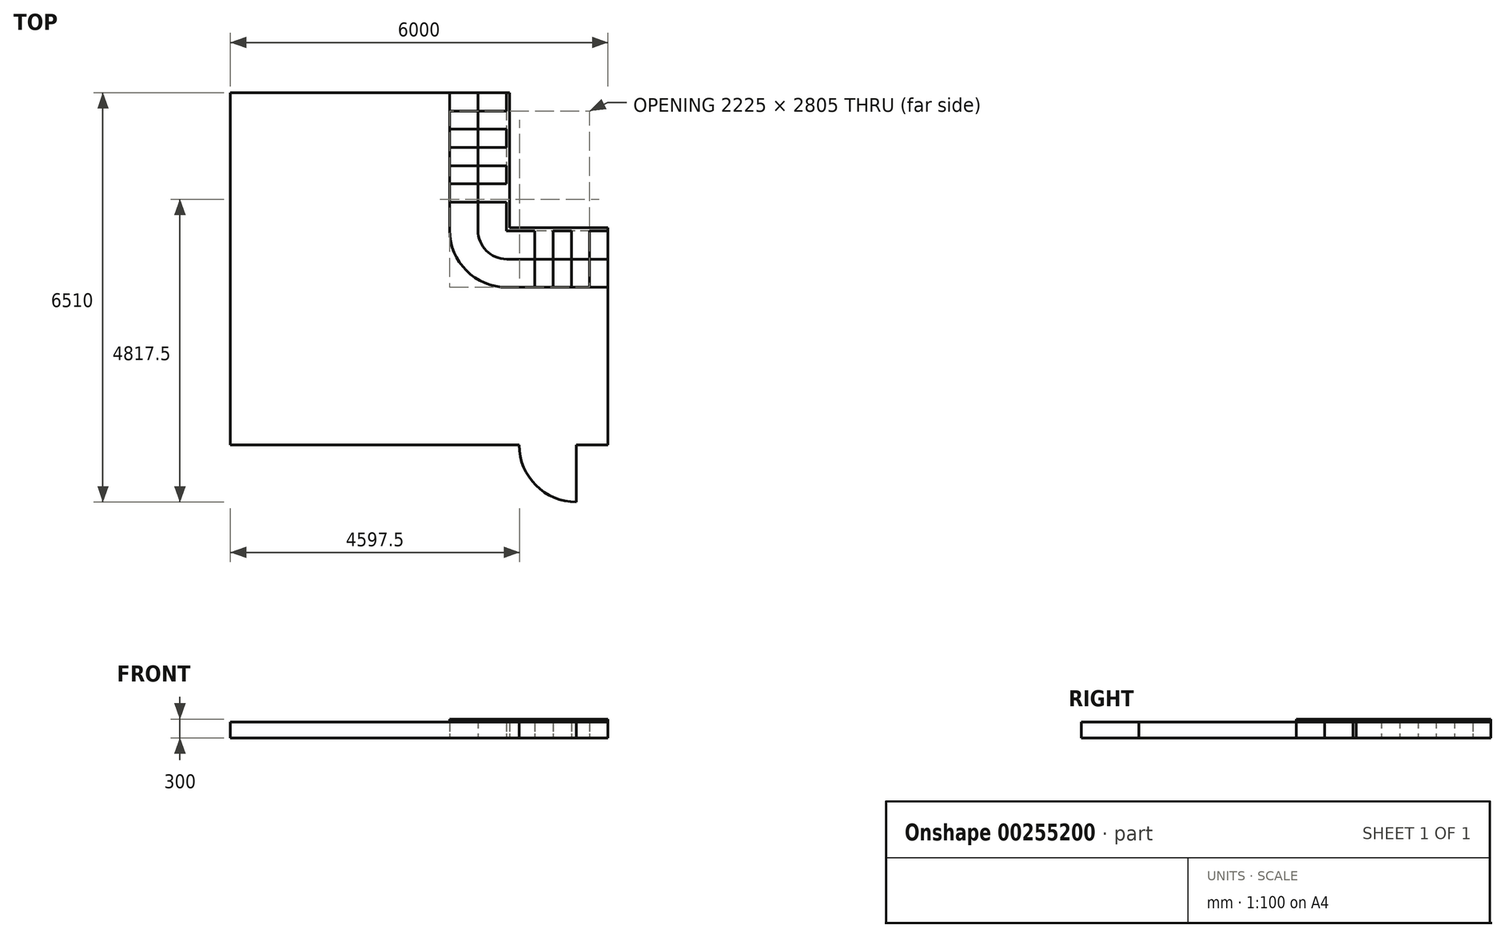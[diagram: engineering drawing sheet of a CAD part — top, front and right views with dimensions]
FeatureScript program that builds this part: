
annotation { "Feature Type Name" : "Feature", "Feature Type Description" : "" }
export const myFeature = defineFeature(function(context is Context, id is Id, definition is map)
    precondition{}
    {
        {
            var Q0;
            Q0=qCreatedBy(makeId("Top.planeOp"),FACE);
            var sketch = newSketch(context, id + "F0", { "sketchPlane" : qUnion([Q0])});
            skLineSegment(sketch, "E0", {"start": v(-4021.26, -49.2) * mm, "end": v(568.74, -49.2) * mm});
            skLineSegment(sketch, "E1", {"start": v(-4021.26, -49.2) * mm, "end": v(-4021.26, 5550.8) * mm});
            skLineSegment(sketch, "E2", {"start": v(-4021.26, 5550.8) * mm, "end": v(-536.26, 5550.8) * mm});
            skLineSegment(sketch, "E3", {"start": v(-536.26, 5550.8) * mm, "end": v(-86.26, 5550.8) * mm});
            skLineSegment(sketch, "E4", {"start": v(-86.26, 5550.8) * mm, "end": v(363.74, 5550.8) * mm});
            skLineSegment(sketch, "E5", {"start": v(-86.26, 5550.8) * mm, "end": v(-86.26, 3810.8) * mm});
            skLineSegment(sketch, "E6", {"start": v(363.74, 5550.8) * mm, "end": v(363.74, 3810.8) * mm});
            skLineSegment(sketch, "E7", {"start": v(363.74, 5550.8) * mm, "end": v(413.74, 5550.8) * mm});
            skLineSegment(sketch, "E8", {"start": v(413.74, 5550.8) * mm, "end": v(413.74, 3810.8) * mm});
            skPoint(sketch, "E9.end.orphan", {"position": v(-536.26, 3810.8) * mm});
            skPoint(sketch, "E10", {"position": v(-536.26, 5260.8) * mm});
            skPoint(sketch, "E11", {"position": v(-536.26, 5550.8) * mm});
            skPoint(sketch, "E12", {"position": v(-536.26, 4970.8) * mm});
            skPoint(sketch, "E13", {"position": v(-536.26, 4680.8) * mm});
            skPoint(sketch, "E14", {"position": v(-536.26, 4390.8) * mm});
            skPoint(sketch, "E15", {"position": v(-536.26, 4100.8) * mm});
            skLineSegment(sketch, "E16", {"start": v(-536.26, 5550.8) * mm, "end": v(-536.26, 3810.8) * mm});
            skLineSegment(sketch, "E17", {"start": v(-536.26, 5260.8) * mm, "end": v(363.74, 5260.8) * mm});
            skLineSegment(sketch, "E18", {"start": v(-536.26, 4970.8) * mm, "end": v(363.74, 4970.8) * mm});
            skLineSegment(sketch, "E19", {"start": v(-536.26, 4680.8) * mm, "end": v(363.74, 4680.8) * mm});
            skLineSegment(sketch, "E20", {"start": v(-536.26, 4390.8) * mm, "end": v(363.74, 4390.8) * mm});
            skLineSegment(sketch, "E21", {"start": v(-536.26, 4100.8) * mm, "end": v(363.74, 4100.8) * mm});
            skLineSegment(sketch, "E22", {"start": v(-536.26, 3810.8) * mm, "end": v(363.74, 3810.8) * mm});
            skLineSegment(sketch, "E23", {"start": v(1478.74, -49.2) * mm, "end": v(1978.74, -49.2) * mm});
            skLineSegment(sketch, "E24", {"start": v(1978.74, -49.2) * mm, "end": v(1978.74, 2455.8) * mm});
            skPoint(sketch, "E25", {"position": v(1978.74, 2455.8) * mm});
            skPoint(sketch, "E26", {"position": v(1688.74, 2455.8) * mm});
            skPoint(sketch, "E27", {"position": v(1398.74, 2455.8) * mm});
            skPoint(sketch, "E28", {"position": v(1108.74, 2455.8) * mm});
            skPoint(sketch, "E29", {"position": v(818.74, 2455.8) * mm});
            skLineSegment(sketch, "E30", {"start": v(1978.74, 2455.8) * mm, "end": v(818.74, 2455.8) * mm});
            skLineSegment(sketch, "E31", {"start": v(1978.74, 2455.8) * mm, "end": v(1978.74, 2905.8) * mm});
            skLineSegment(sketch, "E32", {"start": v(1978.74, 2905.8) * mm, "end": v(1978.74, 3355.8) * mm});
            skLineSegment(sketch, "E33", {"start": v(1978.74, 3355.8) * mm, "end": v(1978.74, 3405.8) * mm});
            skLineSegment(sketch, "E34", {"start": v(1978.74, 2905.8) * mm, "end": v(818.74, 2905.8) * mm});
            skLineSegment(sketch, "E35", {"start": v(1978.74, 3355.8) * mm, "end": v(818.74, 3355.8) * mm});
            skLineSegment(sketch, "E36", {"start": v(1978.74, 3405.8) * mm, "end": v(818.74, 3405.8) * mm});
            skLineSegment(sketch, "E37", {"start": v(1688.74, 2455.8) * mm, "end": v(1688.74, 3355.8) * mm});
            skLineSegment(sketch, "E38", {"start": v(1398.74, 2455.8) * mm, "end": v(1398.74, 3355.8) * mm});
            skLineSegment(sketch, "E39", {"start": v(1108.74, 2455.8) * mm, "end": v(1108.74, 3355.8) * mm});
            skLineSegment(sketch, "E40", {"start": v(818.74, 2455.8) * mm, "end": v(818.74, 3355.8) * mm});
            skPoint(sketch, "E41", {"position": v(363.74, 5260.8) * mm});
            skPoint(sketch, "E42", {"position": v(363.74, 4970.8) * mm});
            skPoint(sketch, "E43", {"position": v(363.74, 4680.8) * mm});
            skPoint(sketch, "E44", {"position": v(363.74, 4390.8) * mm});
            skPoint(sketch, "E45", {"position": v(363.74, 4100.8) * mm});
            skPoint(sketch, "E46", {"position": v(363.74, 3810.8) * mm});
            skPoint(sketch, "E47", {"position": v(363.74, 5550.8) * mm});
            skPoint(sketch, "E48.orphan", {"position": v(413.74, 5260.8) * mm});
            skPoint(sketch, "E49.orphan", {"position": v(413.74, 4970.8) * mm});
            skPoint(sketch, "E50.orphan", {"position": v(413.74, 4680.8) * mm});
            skPoint(sketch, "E51.orphan", {"position": v(413.74, 4390.8) * mm});
            skPoint(sketch, "E52.orphan", {"position": v(413.74, 4100.8) * mm});
            skPoint(sketch, "E53", {"position": v(1688.74, 3355.8) * mm});
            skPoint(sketch, "E54", {"position": v(1398.74, 3355.8) * mm});
            skPoint(sketch, "E55", {"position": v(1108.74, 3355.8) * mm});
            skPoint(sketch, "E56", {"position": v(818.74, 3355.8) * mm});
            skPoint(sketch, "E57.orphan", {"position": v(1398.74, 3405.8) * mm});
            skLineSegment(sketch, "E58", {"start": v(413.74, 3810.8) * mm, "end": v(413.74, 3405.8) * mm});
            skLineSegment(sketch, "E59", {"start": v(818.74, 3405.8) * mm, "end": v(413.74, 3405.8) * mm});
            skLineSegment(sketch, "E60", {"start": v(363.74, 3810.8) * mm, "end": v(363.74, 3355.8) * mm});
            skLineSegment(sketch, "E61", {"start": v(818.74, 3355.8) * mm, "end": v(363.74, 3355.8) * mm});
            skLineSegment(sketch, "E62", {"start": v(-536.26, 3810.8) * mm, "end": v(-536.26, 3365.8) * mm});
            skLineSegment(sketch, "E63", {"start": v(373.74, 2455.8) * mm, "end": v(818.74, 2455.8) * mm});
            skPoint(sketch, "E64", {"position": v(363.74, 3355.8) * mm});
            skPoint(sketch, "E65", {"position": v(363.74, 3405.8) * mm});
            skPoint(sketch, "E66", {"position": v(413.74, 3355.8) * mm});
            skPoint(sketch, "E67.trimOffspring.end.orphan", {"position": v(413.74, 2455.8) * mm});
            skPoint(sketch, "E68.trimOffspring.end.orphan", {"position": v(-536.26, 3405.8) * mm});
            skLineSegment(sketch, "E69", {"start": v(-86.26, 3810.8) * mm, "end": v(-86.26, 3360.8) * mm});
            skLineSegment(sketch, "E70", {"start": v(368.74, 2905.8) * mm, "end": v(818.74, 2905.8) * mm});
            skPoint(sketch, "E71.trimOffspring.end.orphan", {"position": v(-536.26, 3355.8) * mm});
            skPoint(sketch, "E72.trimOffspring.end.orphan", {"position": v(363.74, 2455.8) * mm});
            skPoint(sketch, "E73.visualSharp", {"position": v(-536.26, 2455.8) * mm});
            skPoint(sketch, "E74.orphan", {"position": v(-86.26, 2905.8) * mm});
            skLineSegment(sketch, "E75", {"start": v(-536.26, 3365.8) * mm, "end": v(-536.26, 3355.8) * mm});
            skLineSegment(sketch, "E76", {"start": v(363.74, 2455.8) * mm, "end": v(373.74, 2455.8) * mm});
            skLineSegment(sketch, "E77", {"start": v(368.74, 2905.8) * mm, "end": v(368.74, 2905.8) * mm});
            skLineSegment(sketch, "E78", {"start": v(-86.26, 3360.8) * mm, "end": v(-86.26, 3360.8) * mm});
            skArc(sketch, "E79.filletArc", {"start": v(-86.26, 3360.8) * mm, "mid": v(47, 3039.06) * mm, "end": v(368.74, 2905.8) * mm});
            skArc(sketch, "E80.filletArc", {"start": v(-536.26, 3365.8) * mm, "mid": v(-269.73, 2722.33) * mm, "end": v(373.74, 2455.8) * mm});
            skArc(sketch, "E81", {"start": v(568.74, -49.2) * mm, "mid": v(835.27, -692.67) * mm, "end": v(1478.74, -959.2) * mm});
            skLineSegment(sketch, "E82", {"start": v(1478.74, -49.2) * mm, "end": v(1478.74, -959.2) * mm});
            skSolve(sketch);
        }
        {
            var Q0;
            {var subQ3=sQuery(id+"F0.wireOp",EDGE,"E62");Q0=makeQuery(id+"F0.imprint","IMPRINT",FACE,{"disambiguationData":[TD([[makeQuery(id+"F0.imprint","IMPRINT",EDGE,{"derivedFrom":subQ3}),1.0]])]});}
            var Q1;
            {var subQ6=sQuery(id+"F0.wireOp",EDGE,"E7");Q1=makeQuery(id+"F0.imprint","IMPRINT",FACE,{"disambiguationData":[TD([[makeQuery(id+"F0.imprint","IMPRINT",EDGE,{"derivedFrom":subQ6}),-1.0]])]});}
            var Q2;
            {var subQ0=sQuery(id+"F0.wireOp",EDGE,"E38");var subQ1=sQuery(id+"F0.wireOp",EDGE,"E30");var subQ2=makeQuery(id+"F0.imprint","INTERSECT",VERTEX,{"derivedFrom":[subQ1,subQ0]});Q2=makeQuery(id+"F0.imprint","IMPRINT",FACE,{"disambiguationData":[TD([[makeQuery(id+"F0.imprint","IMPRINT",EDGE,{"disambiguationData":[TD([[subQ2,-1.0]])],"derivedFrom":subQ1}),-1.0]])]});}
            var Q3;
            {var subQ0=sQuery(id+"F0.wireOp",EDGE,"E20");var subQ1=sQuery(id+"F0.wireOp",EDGE,"E5");var subQ2=makeQuery(id+"F0.imprint","INTERSECT",VERTEX,{"derivedFrom":[subQ1,subQ0]});Q3=makeQuery(id+"F0.imprint","IMPRINT",FACE,{"disambiguationData":[TD([[makeQuery(id+"F0.imprint","IMPRINT",EDGE,{"disambiguationData":[TD([[subQ2,-1.0]])],"derivedFrom":subQ1}),-1.0]])]});}
            var Q4;
            {var subQ0=sQuery(id+"F0.wireOp",EDGE,"E3");Q4=makeQuery(id+"F0.imprint","IMPRINT",FACE,{"disambiguationData":[TD([[makeQuery(id+"F0.imprint","IMPRINT",EDGE,{"derivedFrom":subQ0}),-1.0]])]});}
            var Q5;
            {var subQ0=sQuery(id+"F0.wireOp",EDGE,"E31");Q5=makeQuery(id+"F0.imprint","IMPRINT",FACE,{"disambiguationData":[TD([[makeQuery(id+"F0.imprint","IMPRINT",EDGE,{"derivedFrom":subQ0}),1.0]])]});}
            var Q6;
            {var subQ0=sQuery(id+"F0.wireOp",EDGE,"E18");var subQ1=sQuery(id+"F0.wireOp",EDGE,"E5");var subQ2=makeQuery(id+"F0.imprint","INTERSECT",VERTEX,{"derivedFrom":[subQ1,subQ0]});Q6=makeQuery(id+"F0.imprint","IMPRINT",FACE,{"disambiguationData":[TD([[makeQuery(id+"F0.imprint","IMPRINT",EDGE,{"disambiguationData":[TD([[subQ2,-1.0]])],"derivedFrom":subQ1}),-1.0]])]});}
            var Q7;
            {var subQ0=sQuery(id+"F0.wireOp",EDGE,"E17");var subQ1=sQuery(id+"F0.wireOp",EDGE,"E5");var subQ2=makeQuery(id+"F0.imprint","INTERSECT",VERTEX,{"derivedFrom":[subQ1,subQ0]});Q7=makeQuery(id+"F0.imprint","IMPRINT",FACE,{"disambiguationData":[TD([[makeQuery(id+"F0.imprint","IMPRINT",EDGE,{"disambiguationData":[TD([[subQ2,-1.0]])],"derivedFrom":subQ1}),1.0]])]});}
            var Q8;
            {var subQ0=sQuery(id+"F0.wireOp",EDGE,"E19");var subQ1=sQuery(id+"F0.wireOp",EDGE,"E5");var subQ2=makeQuery(id+"F0.imprint","INTERSECT",VERTEX,{"derivedFrom":[subQ1,subQ0]});Q8=makeQuery(id+"F0.imprint","IMPRINT",FACE,{"disambiguationData":[TD([[makeQuery(id+"F0.imprint","IMPRINT",EDGE,{"disambiguationData":[TD([[subQ2,-1.0]])],"derivedFrom":subQ1}),1.0]])]});}
            var Q9;
            {var subQ3=sQuery(id+"F0.wireOp",EDGE,"E21");var subQ5=sQuery(id+"F0.wireOp",EDGE,"E6");var subQ7=makeQuery(id+"F0.imprint","INTERSECT",VERTEX,{"derivedFrom":[subQ5,subQ3]});Q9=makeQuery(id+"F0.imprint","IMPRINT",FACE,{"disambiguationData":[TD([[makeQuery(id+"F0.imprint","IMPRINT",EDGE,{"disambiguationData":[TD([[subQ7,1.0]])],"derivedFrom":subQ3}),-1.0]])]});}
            var Q10;
            {var subQ3=sQuery(id+"F0.wireOp",EDGE,"E39");var subQ5=sQuery(id+"F0.wireOp",EDGE,"E35");var subQ7=makeQuery(id+"F0.imprint","INTERSECT",VERTEX,{"derivedFrom":[subQ5,subQ3]});Q10=makeQuery(id+"F0.imprint","IMPRINT",FACE,{"disambiguationData":[TD([[makeQuery(id+"F0.imprint","IMPRINT",EDGE,{"disambiguationData":[TD([[subQ7,1.0]])],"derivedFrom":subQ3}),1.0]])]});}
            var Q11;
            {var subQ0=sQuery(id+"F0.wireOp",EDGE,"E37");var subQ1=sQuery(id+"F0.wireOp",EDGE,"E34");var subQ2=makeQuery(id+"F0.imprint","INTERSECT",VERTEX,{"derivedFrom":[subQ1,subQ0]});Q11=makeQuery(id+"F0.imprint","IMPRINT",FACE,{"disambiguationData":[TD([[makeQuery(id+"F0.imprint","IMPRINT",EDGE,{"disambiguationData":[TD([[subQ2,-1.0]])],"derivedFrom":subQ1}),-1.0]])]});}
            extrude(context, id + "F1", {"entities" : qUnion([Q0, Q1, Q2, Q3, Q4, Q5, Q6, Q7, Q8, Q9, Q10, Q11]), "depth" : 300 * mm});
        }
        {
            var Q0;
            Q0 = qSketchRegion(id + "F0", true);
            extrude(context, id + "F2", {"entities" : qUnion([Q0]), "depth" : 250 * mm});
        }
    });
